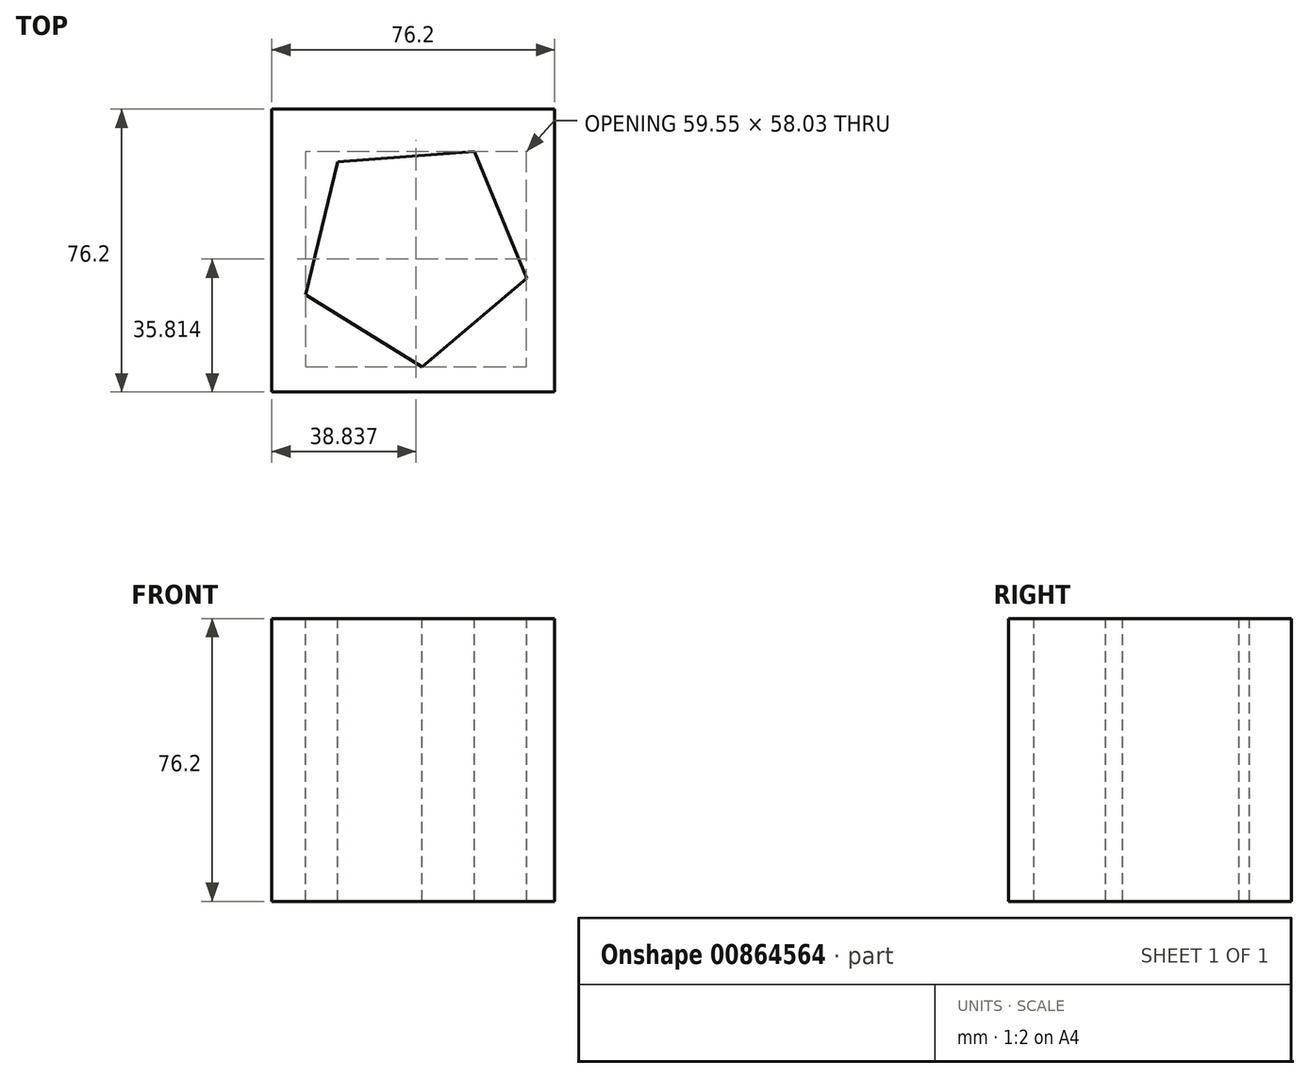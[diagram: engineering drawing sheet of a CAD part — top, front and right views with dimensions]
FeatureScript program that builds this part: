
annotation { "Feature Type Name" : "Feature", "Feature Type Description" : "" }
export const myFeature = defineFeature(function(context is Context, id is Id, definition is map)
    precondition{}
    {
        {
            var Q0;
            Q0=qCreatedBy(makeId("Top.planeOp"),FACE);
            var sketch = newSketch(context, id + "F0", { "sketchPlane" : qUnion([Q0])});
            skLineSegment(sketch, "E0.bottom", {"start": v(-58.18, 49.87) * mm, "end": v(18.02, 49.87) * mm});
            skLineSegment(sketch, "E0.top", {"start": v(-58.18, -26.33) * mm, "end": v(18.02, -26.33) * mm});
            skLineSegment(sketch, "E0.left", {"start": v(-58.18, 49.87) * mm, "end": v(-58.18, -26.33) * mm});
            skLineSegment(sketch, "E0.right", {"start": v(18.02, 49.87) * mm, "end": v(18.02, -26.33) * mm});
            skSolve(sketch);
        }
        {
            var Q0;
            Q0=makeQuery(id+"F0.imprint","IMPRINT",FACE,{"disambiguationData":[TD([[makeQuery(id+"F0.imprint","IMPRINT",EDGE,{"derivedFrom":sQuery(id+"F0.wireOp",EDGE,"E0.bottom")}),-1.0]])]});
            extrude(context, id + "F1", {"entities" : qUnion([Q0]), "depth" : 76.2 * mm, "offsetDistance" : 25.4 * mm});
        }
        {
            var Q0;
            Q0=makeQuery(id+"F1.opExtrude","CAP_FACE",FACE,{"disambiguationData":[OSD([sQuery(id+"F0.wireOp",EDGE,"E0.bottom"),sQuery(id+"F0.wireOp",EDGE,"E0.top"),sQuery(id+"F0.wireOp",EDGE,"E0.left"),sQuery(id+"F0.wireOp",EDGE,"E0.right")])],"isStart":false});
            var sketch = newSketch(context, id + "F2", { "sketchPlane" : qUnion([Q0])});
            skCircle(sketch, "E1.cCircle", {"center": v(-20.08, 11.77) * mm, "radius": 25.4 * mm, "construction": true});
            skLineSegment(sketch, "E1.0", {"start": v(10.43, 4.36) * mm, "end": v(-17.7, -19.53) * mm});
            skLineSegment(sketch, "E1.1", {"start": v(-17.7, -19.53) * mm, "end": v(-49.12, -0.16) * mm});
            skLineSegment(sketch, "E1.2", {"start": v(-49.12, -0.16) * mm, "end": v(-40.4, 35.7) * mm});
            skLineSegment(sketch, "E1.3", {"start": v(-40.4, 35.7) * mm, "end": v(-3.6, 38.5) * mm});
            skLineSegment(sketch, "E1.4", {"start": v(-3.6, 38.5) * mm, "end": v(10.43, 4.36) * mm});
            skPoint(sketch, "E1.0.midPoint", {"position": v(-3.63, -7.58) * mm});
            skSolve(sketch);
        }
        {
            var Q0;
            Q0 = qSketchRegion(id + "F2", true);
            extrude(context, id + "F3", {"entities" : qUnion([Q0]), "operationType" : NewBodyOperationType.REMOVE, "endBound" : BoundingType.THROUGH_ALL, "oppositeDirection" : true, "depth" : 25.4 * mm, "offsetDistance" : 25.4 * mm});
        }
    });
